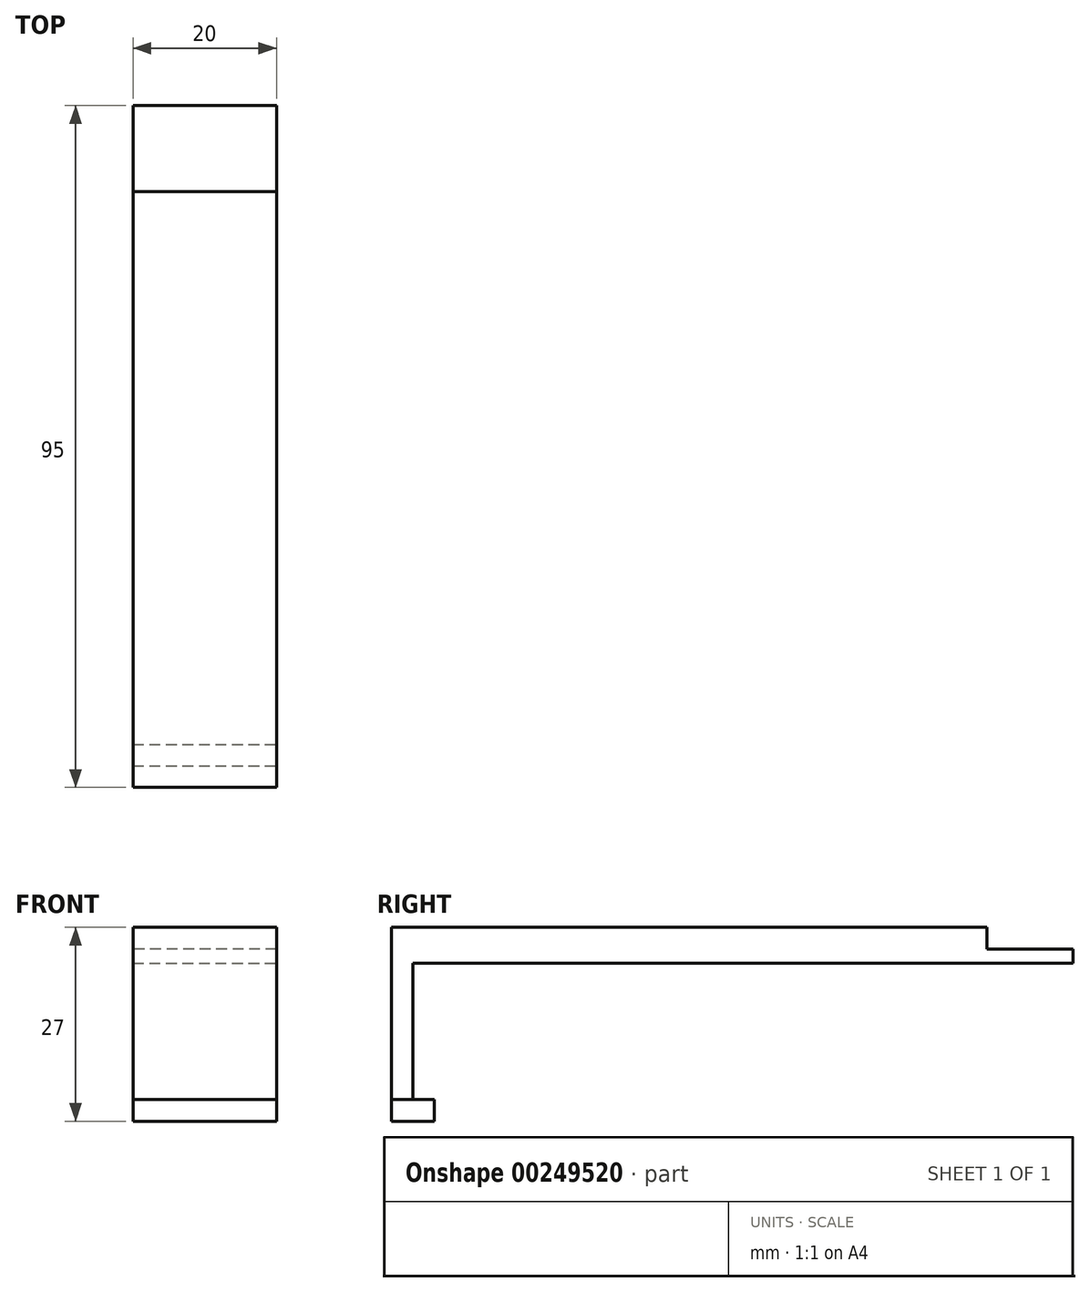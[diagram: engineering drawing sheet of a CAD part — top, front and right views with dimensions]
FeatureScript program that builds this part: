
annotation { "Feature Type Name" : "Feature", "Feature Type Description" : "" }
export const myFeature = defineFeature(function(context is Context, id is Id, definition is map)
    precondition{}
    {
        {
            var Q0;
            Q0=qCreatedBy(makeId("Top.planeOp"),FACE);
            var sketch = newSketch(context, id + "F0", { "sketchPlane" : qUnion([Q0])});
            skLineSegment(sketch, "E0.bottom", {"start": v(10, -47.5) * mm, "end": v(-10, -47.5) * mm});
            skLineSegment(sketch, "E0.top", {"start": v(10, 47.5) * mm, "end": v(-10, 47.5) * mm});
            skLineSegment(sketch, "E0.left", {"start": v(10, -47.5) * mm, "end": v(10, 47.5) * mm});
            skLineSegment(sketch, "E0.right", {"start": v(-10, -47.5) * mm, "end": v(-10, 47.5) * mm});
            skPoint(sketch, "E0.middle", {"position": v(0, 0) * mm});
            skLineSegment(sketch, "E1", {"start": v(-10, -47.5) * mm, "end": v(-10, -44.5) * mm});
            skLineSegment(sketch, "E2", {"start": v(10, -47.5) * mm, "end": v(10, -44.5) * mm});
            skLineSegment(sketch, "E3", {"start": v(10, -44.5) * mm, "end": v(10, -41.5) * mm});
            skLineSegment(sketch, "E4", {"start": v(-10, -44.5) * mm, "end": v(-10, -41.5) * mm});
            skLineSegment(sketch, "E5", {"start": v(-10, -41.5) * mm, "end": v(10, -41.5) * mm});
            skLineSegment(sketch, "E6", {"start": v(-10, -44.5) * mm, "end": v(10, -44.5) * mm});
            skLineSegment(sketch, "E7", {"start": v(10, 47.5) * mm, "end": v(10, 35.5) * mm});
            skLineSegment(sketch, "E8", {"start": v(10, 35.5) * mm, "end": v(-10, 35.5) * mm});
            skSolve(sketch);
        }
        {
            var Q0;
            {var subQ0=sQuery(id+"F0.wireOp",EDGE,"E0.bottom");Q0=makeQuery(id+"F0.imprint","IMPRINT",FACE,{"disambiguationData":[TD([[makeQuery(id+"F0.imprint","IMPRINT",EDGE,{"derivedFrom":subQ0}),-1.0]])]});}
            extrude(context, id + "F1", {"entities" : qUnion([Q0]), "oppositeDirection" : true, "depth" : 24 * mm});
        }
        {
            var Q0;
            {var subQ0=sQuery(id+"F0.wireOp",EDGE,"E5");Q0=makeQuery(id+"F0.imprint","IMPRINT",FACE,{"disambiguationData":[TD([[makeQuery(id+"F0.imprint","IMPRINT",EDGE,{"derivedFrom":subQ0}),-1.0]])]});}
            var Q1;
            {var subQ0=sQuery(id+"F0.wireOp",EDGE,"E0.bottom");Q1=makeQuery(id+"F0.imprint","IMPRINT",FACE,{"disambiguationData":[TD([[makeQuery(id+"F0.imprint","IMPRINT",EDGE,{"derivedFrom":subQ0}),-1.0]])]});}
            extrude(context, id + "F2", {"entities" : qUnion([Q0, Q1]), "oppositeDirection" : true, "depth" : 3 * mm});
        }
        {
            var Q0;
            Q0=makeQuery(id+"F2.opExtrude","SWEPT_BODY",BODY,{"disambiguationData":[OSD([sQuery(id+"F0.wireOp",EDGE,"E0.bottom"),sQuery(id+"F0.wireOp",EDGE,"E0.left"),sQuery(id+"F0.wireOp",EDGE,"E0.right"),sQuery(id+"F0.wireOp",EDGE,"E5")])]});
            var Q1;
            Q1=makeQuery(id+"F1.opExtrude","SWEPT_EDGE",EDGE,{"disambiguationData":[OSD([sQuery(id+"F0.wireOp",EDGE,"E0.bottom"),sQuery(id+"F0.wireOp",EDGE,"E0.right")])]});
            transform(context, id + "F3", {"entities" : qUnion([Q0]), "transformType" : TransformType.TRANSLATION_ENTITY, "oppositeDirectionEntity" : true, "transformLine" : qUnion([Q1]), "makeCopy" : false});
        }
        {
            var Q0;
            {var subQ0=sQuery(id+"F0.wireOp",EDGE,"E5");Q0=makeQuery(id+"F0.imprint","IMPRINT",FACE,{"disambiguationData":[TD([[makeQuery(id+"F0.imprint","IMPRINT",EDGE,{"derivedFrom":subQ0}),-1.0]])]});}
            var Q1;
            {var subQ0=sQuery(id+"F0.wireOp",EDGE,"E5");Q1=makeQuery(id+"F0.imprint","IMPRINT",FACE,{"disambiguationData":[TD([[makeQuery(id+"F0.imprint","IMPRINT",EDGE,{"derivedFrom":subQ0}),1.0]])]});}
            var Q2;
            {var subQ0=sQuery(id+"F0.wireOp",EDGE,"E0.top");Q2=makeQuery(id+"F0.imprint","IMPRINT",FACE,{"disambiguationData":[TD([[makeQuery(id+"F0.imprint","IMPRINT",EDGE,{"derivedFrom":subQ0}),1.0]])]});}
            extrude(context, id + "F4", {"entities" : qUnion([Q0, Q1, Q2]), "operationType" : NewBodyOperationType.ADD, "oppositeDirection" : true, "depth" : 5 * mm});
        }
        {
            var Q0;
            {var subQ0=sQuery(id+"F0.wireOp",EDGE,"E0.top");Q0=makeQuery(id+"F0.imprint","IMPRINT",FACE,{"disambiguationData":[TD([[makeQuery(id+"F0.imprint","IMPRINT",EDGE,{"derivedFrom":subQ0}),1.0]])]});}
            extrude(context, id + "F5", {"entities" : qUnion([Q0]), "operationType" : NewBodyOperationType.REMOVE, "oppositeDirection" : true, "depth" : 3 * mm});
        }
    });
